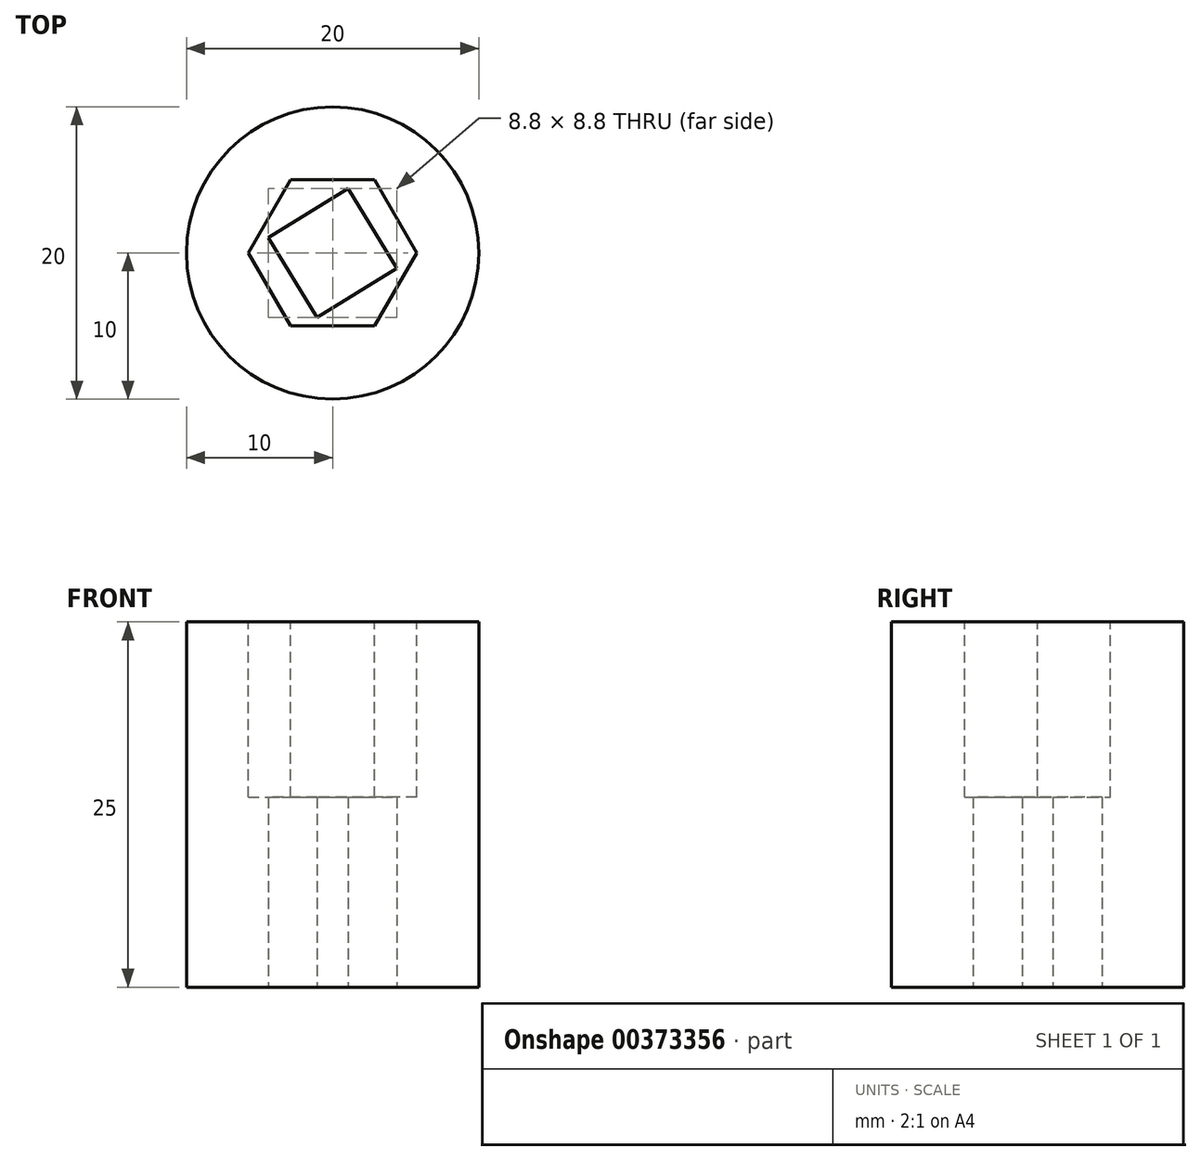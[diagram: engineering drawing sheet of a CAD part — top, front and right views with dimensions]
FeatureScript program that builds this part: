
annotation { "Feature Type Name" : "Feature", "Feature Type Description" : "" }
export const myFeature = defineFeature(function(context is Context, id is Id, definition is map)
    precondition{}
    {
        {
            var Q0;
            Q0=qCreatedBy(makeId("Top.planeOp"),FACE);
            var sketch = newSketch(context, id + "F0", { "sketchPlane" : qUnion([Q0])});
            skCircle(sketch, "E0", {"center": v(0, 0) * mm, "radius": 10 * mm});
            skSolve(sketch);
        }
        {
            var Q0;
            Q0=makeQuery(id+"F0.imprint","IMPRINT",FACE,{"disambiguationData":[TD([[makeQuery(id+"F0.imprint","IMPRINT",EDGE,{"derivedFrom":sQuery(id+"F0.wireOp",EDGE,"E0")}),1.0]])]});
            extrude(context, id + "F1", {"entities" : qUnion([Q0]), "depth" : 25 * mm});
        }
        {
            var Q0;
            Q0=makeQuery(id+"F1.opExtrude","CAP_FACE",FACE,{"disambiguationData":[OSD([sQuery(id+"F0.wireOp",EDGE,"E0")])],"isStart":false});
            var sketch = newSketch(context, id + "F2", { "sketchPlane" : qUnion([Q0])});
            skCircle(sketch, "E1.cCircle", {"center": v(0, 0) * mm, "radius": 5 * mm, "construction": true});
            skLineSegment(sketch, "E1.0", {"start": v(-2.89, 5) * mm, "end": v(2.89, 5) * mm});
            skLineSegment(sketch, "E1.1", {"start": v(2.89, 5) * mm, "end": v(5.77, 0) * mm});
            skLineSegment(sketch, "E1.2", {"start": v(5.77, 0) * mm, "end": v(2.89, -5) * mm});
            skLineSegment(sketch, "E1.3", {"start": v(2.89, -5) * mm, "end": v(-2.89, -5) * mm});
            skLineSegment(sketch, "E1.4", {"start": v(-2.89, -5) * mm, "end": v(-5.77, 0) * mm});
            skLineSegment(sketch, "E1.5", {"start": v(-5.77, 0) * mm, "end": v(-2.89, 5) * mm});
            skPoint(sketch, "E1.0.midPoint", {"position": v(0, 5) * mm});
            skSolve(sketch);
        }
        {
            var Q0;
            Q0 = qSketchRegion(id + "F2", true);
            extrude(context, id + "F3", {"entities" : qUnion([Q0]), "operationType" : NewBodyOperationType.REMOVE, "oppositeDirection" : true, "depth" : 12 * mm});
        }
        {
            var Q0;
            Q0=makeQuery(id+"F1.opExtrude","CAP_FACE",FACE,{"disambiguationData":[OSD([sQuery(id+"F0.wireOp",EDGE,"E0")])],"isStart":true});
            var sketch = newSketch(context, id + "F4", { "sketchPlane" : qUnion([Q0])});
            skCircle(sketch, "E2.cCircle", {"center": v(0, 0) * mm, "radius": 3.2 * mm, "construction": true});
            skLineSegment(sketch, "E2.0", {"start": v(4.4, 1.06) * mm, "end": v(1.06, -4.4) * mm});
            skLineSegment(sketch, "E2.1", {"start": v(1.06, -4.4) * mm, "end": v(-4.4, -1.06) * mm});
            skLineSegment(sketch, "E2.2", {"start": v(-4.4, -1.06) * mm, "end": v(-1.06, 4.4) * mm});
            skLineSegment(sketch, "E2.3", {"start": v(-1.06, 4.4) * mm, "end": v(4.4, 1.06) * mm});
            skPoint(sketch, "E2.0.midPoint", {"position": v(2.73, -1.67) * mm});
            skSolve(sketch);
        }
        {
            var Q0;
            Q0 = qSketchRegion(id + "F4", true);
            extrude(context, id + "F5", {"entities" : qUnion([Q0]), "operationType" : NewBodyOperationType.REMOVE, "oppositeDirection" : true, "depth" : 25 * mm});
        }
    });
